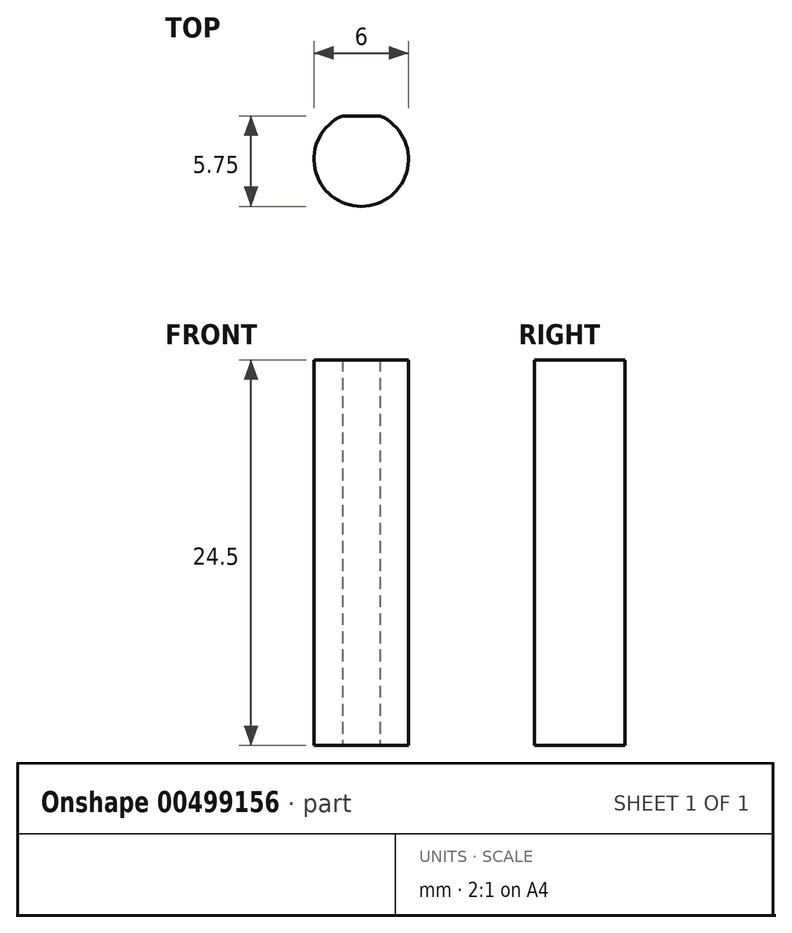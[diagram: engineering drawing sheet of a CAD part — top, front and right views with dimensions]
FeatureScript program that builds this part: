
annotation { "Feature Type Name" : "Feature", "Feature Type Description" : "" }
export const myFeature = defineFeature(function(context is Context, id is Id, definition is map)
    precondition{}
    {
        {
            var Q0;
            Q0=qCreatedBy(makeId("Top.planeOp"),FACE);
            var sketch = newSketch(context, id + "F0", { "sketchPlane" : qUnion([Q0])});
            skLineSegment(sketch, "E0.bottom", {"start": v(1.2, 2.75) * mm, "end": v(-1.2, 2.75) * mm});
            skLineSegment(sketch, "E0.top", {"start": v(1.2, -2.75) * mm, "end": v(-1.2, -2.75) * mm, "construction": true});
            skLineSegment(sketch, "E0.left", {"start": v(1.2, 2.75) * mm, "end": v(1.2, -2.75) * mm, "construction": true});
            skLineSegment(sketch, "E0.right", {"start": v(-1.2, 2.75) * mm, "end": v(-1.2, -2.75) * mm, "construction": true});
            skPoint(sketch, "E0.middle", {"position": v(0, 0) * mm});
            skArc(sketch, "E1", {"start": v(-1.2, 2.75) * mm, "mid": v(0, -3) * mm, "end": v(1.2, 2.75) * mm});
            skArc(sketch, "E2", {"start": v(1.2, 2.75) * mm, "mid": v(0, 3) * mm, "end": v(-1.2, 2.75) * mm, "construction": true});
            skSolve(sketch);
        }
        {
            var Q0;
            Q0=makeQuery(id+"F0.imprint","IMPRINT",FACE,{"disambiguationData":[TD([[makeQuery(id+"F0.imprint","IMPRINT",EDGE,{"derivedFrom":sQuery(id+"F0.wireOp",EDGE,"E0.bottom")}),1.0]])]});
            extrude(context, id + "F1", {"entities" : qUnion([Q0]), "depth" : 24.5 * mm});
        }
    });
